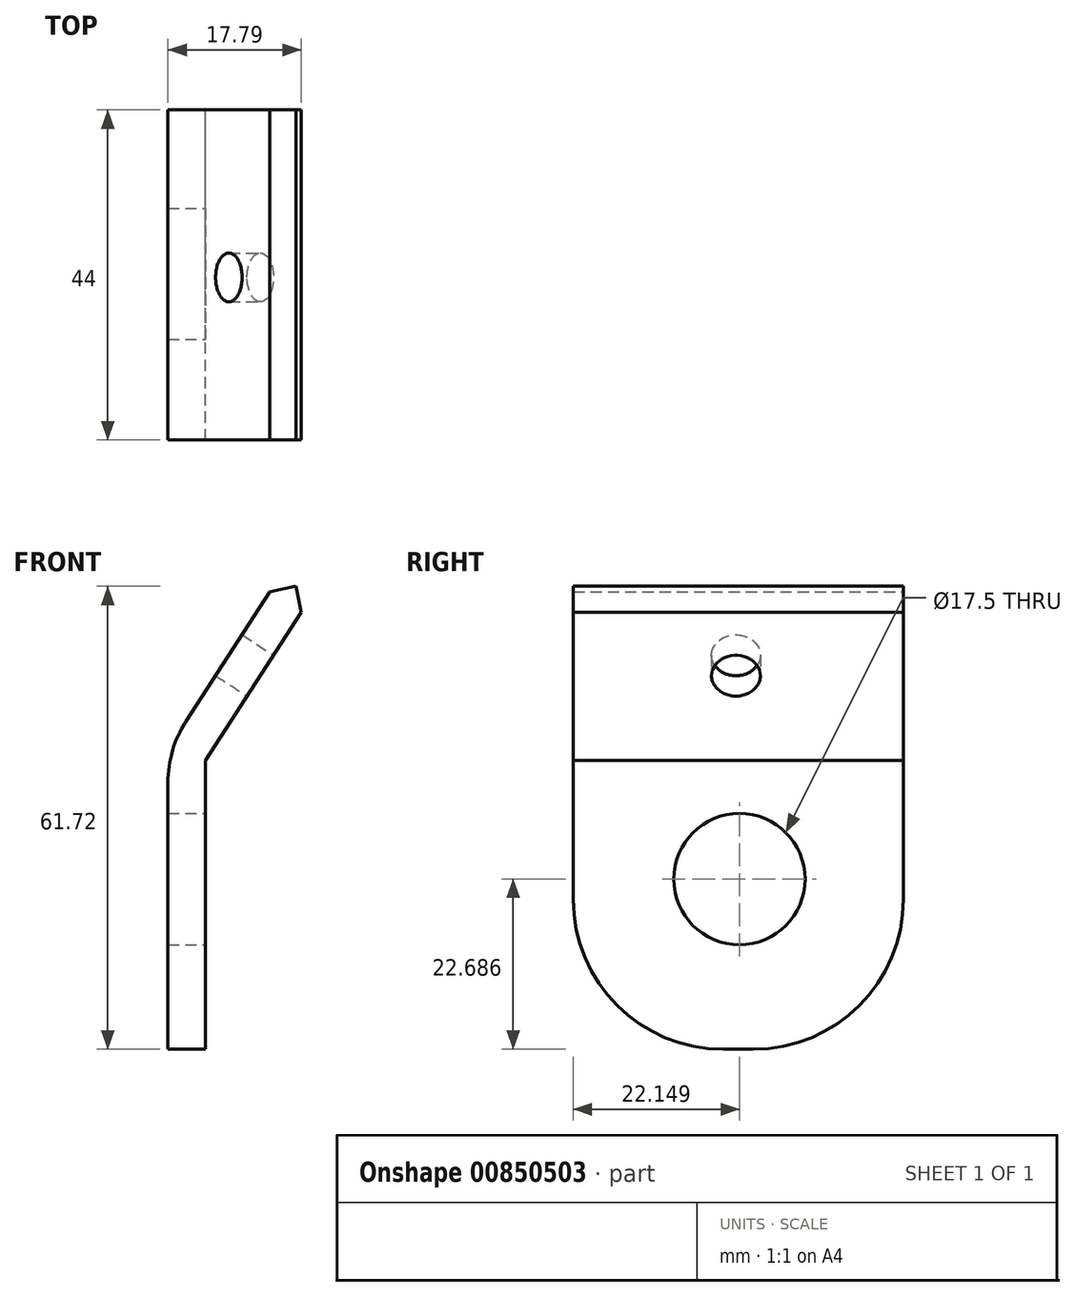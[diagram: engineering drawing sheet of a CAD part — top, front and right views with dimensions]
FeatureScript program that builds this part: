
annotation { "Feature Type Name" : "Feature", "Feature Type Description" : "" }
export const myFeature = defineFeature(function(context is Context, id is Id, definition is map)
    precondition{}
    {
        {
            var Q0;
            Q0=qCreatedBy(makeId("Front.planeOp"),FACE);
            var sketch = newSketch(context, id + "F0", { "sketchPlane" : qUnion([Q0])});
            skLineSegment(sketch, "E0", {"start": v(13.15, 28.49) * mm, "end": v(13.15, -11.51) * mm});
            skLineSegment(sketch, "E1", {"start": v(13.15, 28.49) * mm, "end": v(29.47, 53.66) * mm});
            skLineSegment(sketch, "E2.0", {"start": v(18.15, 27) * mm, "end": v(33.66, 50.94) * mm});
            skLineSegment(sketch, "E2.1", {"start": v(18.15, 27) * mm, "end": v(18.15, -11.51) * mm});
            skLineSegment(sketch, "E3", {"start": v(29.47, 53.66) * mm, "end": v(33.66, 50.94) * mm});
            skLineSegment(sketch, "E4", {"start": v(13.15, -11.51) * mm, "end": v(18.15, -11.51) * mm});
            skSolve(sketch);
        }
        {
            var Q0;
            Q0=makeQuery(id+"F0.imprint","IMPRINT",FACE,{"disambiguationData":[TD([[makeQuery(id+"F0.imprint","IMPRINT",EDGE,{"derivedFrom":sQuery(id+"F0.wireOp",EDGE,"E0")}),1.0]])]});
            extrude(context, id + "F1", {"entities" : qUnion([Q0]), "depth" : 44 * mm, "offsetDistance" : 25 * mm});
        }
        {
            var Q0;
            Q0=makeQuery(id+"F1.opExtrude","SWEPT_EDGE",EDGE,{"disambiguationData":[OSD([sQuery(id+"F0.wireOp",EDGE,"E0"),sQuery(id+"F0.wireOp",EDGE,"E1")])]});
            fillet(context, id + "F2", {"entities" : qUnion([Q0]), "radius" : 15 * mm, "tangentPropagation" : true, "allowEdgeOverflow" : false});
        }
        {
            var Q0;
            Q0=makeQuery(id+"F1.opExtrude","SWEPT_EDGE",EDGE,{"disambiguationData":[OSD([sQuery(id+"F0.wireOp",EDGE,"E1"),sQuery(id+"F0.wireOp",EDGE,"E3")])]});
            var Q1;
            Q1=makeQuery(id+"F1.opExtrude","SWEPT_EDGE",EDGE,{"disambiguationData":[OSD([sQuery(id+"F0.wireOp",EDGE,"E2.0"),sQuery(id+"F0.wireOp",EDGE,"E3")])]});
            chamfer(context, id + "F3", {"entities" : qUnion([Q0, Q1]), "width" : 5 * mm, "tangentPropagation" : true});
        }
        {
            var Q0;
            Q0=makeQuery(id+"F1.opExtrude","CAP_EDGE",EDGE,{"disambiguationData":[OSD([sQuery(id+"F0.wireOp",EDGE,"E4")])],"isStart":false});
            var Q1;
            Q1=makeQuery(id+"F1.opExtrude","CAP_EDGE",EDGE,{"disambiguationData":[OSD([sQuery(id+"F0.wireOp",EDGE,"E4")])],"isStart":true});
            fillet(context, id + "F4", {"entities" : qUnion([Q0, Q1]), "radius" : 20 * mm, "tangentPropagation" : true, "allowEdgeOverflow" : false});
        }
        {
            var Q0;
            Q0=makeQuery(id+"F1.opExtrude","SWEPT_FACE",FACE,{"disambiguationData":[OSD([sQuery(id+"F0.wireOp",EDGE,"E2.1")])]});
            var sketch = newSketch(context, id + "F5", { "sketchPlane" : qUnion([Q0])});
            skCircle(sketch, "E5", {"center": v(-21.85, 11.18) * mm, "radius": 8.75 * mm});
            skSolve(sketch);
        }
        {
            var Q0;
            Q0=makeQuery(id+"F5.imprint","IMPRINT",FACE,{"disambiguationData":[TD([[makeQuery(id+"F5.imprint","IMPRINT",EDGE,{"derivedFrom":sQuery(id+"F5.wireOp",EDGE,"E5")}),1.0]])]});
            extrude(context, id + "F6", {"entities" : qUnion([Q0]), "operationType" : NewBodyOperationType.REMOVE, "oppositeDirection" : true, "depth" : 25 * mm, "offsetDistance" : 25 * mm});
        }
        {
            var Q0;
            Q0=makeQuery(id+"F1.opExtrude","SWEPT_FACE",FACE,{"disambiguationData":[OSD([sQuery(id+"F0.wireOp",EDGE,"E2.0")])]});
            var sketch = newSketch(context, id + "F7", { "sketchPlane" : qUnion([Q0])});
            skCircle(sketch, "E6", {"center": v(-22.31, 46) * mm, "radius": 3.25 * mm});
            skSolve(sketch);
        }
        {
            var Q0;
            Q0=makeQuery(id+"F7.imprint","IMPRINT",FACE,{"disambiguationData":[TD([[makeQuery(id+"F7.imprint","IMPRINT",EDGE,{"derivedFrom":sQuery(id+"F7.wireOp",EDGE,"E6")}),1.0]])]});
            extrude(context, id + "F8", {"entities" : qUnion([Q0]), "operationType" : NewBodyOperationType.REMOVE, "oppositeDirection" : true, "depth" : 25 * mm, "offsetDistance" : 25 * mm});
        }
    });
